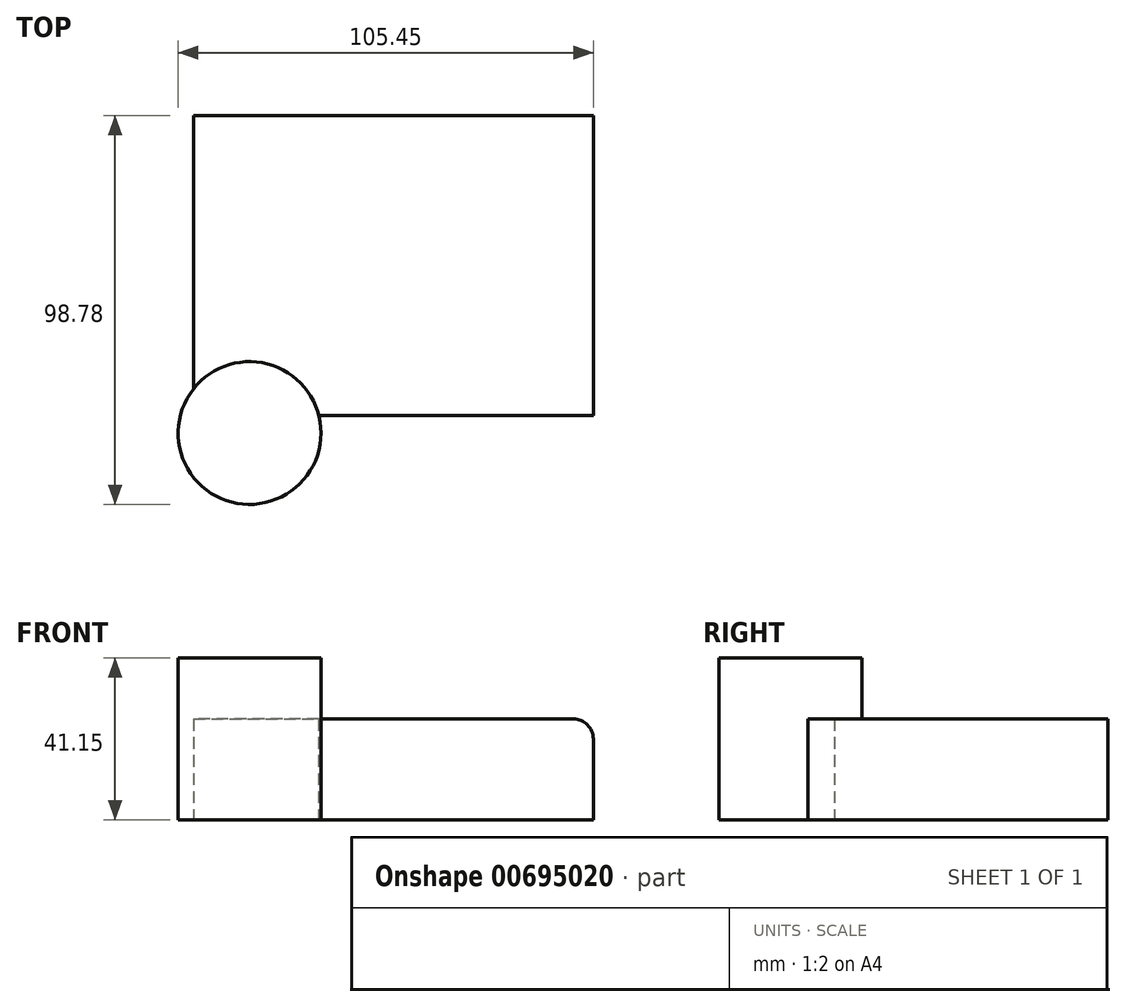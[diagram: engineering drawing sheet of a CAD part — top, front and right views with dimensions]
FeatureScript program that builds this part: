
annotation { "Feature Type Name" : "Feature", "Feature Type Description" : "" }
export const myFeature = defineFeature(function(context is Context, id is Id, definition is map)
    precondition{}
    {
        {
            var Q0;
            Q0=qCreatedBy(makeId("Top.planeOp"),FACE);
            var sketch = newSketch(context, id + "F0", { "sketchPlane" : qUnion([Q0])});
            skLineSegment(sketch, "E0.bottom", {"start": v(-50.28, -33.23) * mm, "end": v(51.32, -33.23) * mm});
            skLineSegment(sketch, "E0.top", {"start": v(-50.28, 42.97) * mm, "end": v(51.32, 42.97) * mm});
            skLineSegment(sketch, "E0.left", {"start": v(-50.28, -33.23) * mm, "end": v(-50.28, 42.97) * mm});
            skLineSegment(sketch, "E0.right", {"start": v(51.32, -33.23) * mm, "end": v(51.32, 42.97) * mm});
            skSolve(sketch);
        }
        {
            var Q0;
            Q0=makeQuery(id+"F0.imprint","IMPRINT",FACE,{"disambiguationData":[TD([[makeQuery(id+"F0.imprint","IMPRINT",EDGE,{"derivedFrom":sQuery(id+"F0.wireOp",EDGE,"E0.bottom")}),1.0]])]});
            extrude(context, id + "F1", {"entities" : qUnion([Q0]), "depth" : 25.65 * mm, "offsetDistance" : 25.4 * mm});
        }
        {
            var Q0;
            Q0=makeQuery(id+"F1.opExtrude","CAP_EDGE",EDGE,{"disambiguationData":[OSD([sQuery(id+"F0.wireOp",EDGE,"E0.right")])],"isStart":false});
            fillet(context, id + "F2", {"entities" : qUnion([Q0]), "radius" : 5.08 * mm, "tangentPropagation" : true, "allowEdgeOverflow" : false});
        }
        {
            var Q0;
            Q0=qCreatedBy(makeId("Top.planeOp"),FACE);
            var sketch = newSketch(context, id + "F3", { "sketchPlane" : qUnion([Q0])});
            skCircle(sketch, "E1", {"center": v(-36, -37.68) * mm, "radius": 18.14 * mm});
            skSolve(sketch);
        }
        {
            var Q0;
            Q0=makeQuery(id+"F3.imprint","IMPRINT",FACE,{"disambiguationData":[TD([[makeQuery(id+"F3.imprint","IMPRINT",EDGE,{"derivedFrom":sQuery(id+"F3.wireOp",EDGE,"E1")}),1.0]])]});
            extrude(context, id + "F4", {"entities" : qUnion([Q0]), "operationType" : NewBodyOperationType.ADD, "depth" : 41.15 * mm, "offsetDistance" : 25.4 * mm});
        }
    });
